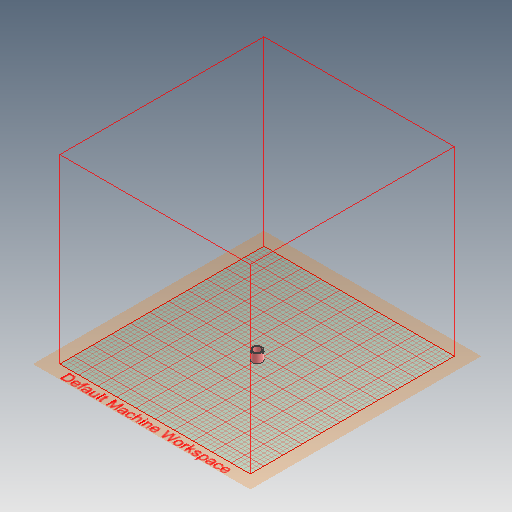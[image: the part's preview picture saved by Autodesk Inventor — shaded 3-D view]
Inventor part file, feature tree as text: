
AUTODESK INVENTOR PART (.ipt)
format: ipt  version: 2021 (Build 250183000, 183)  size: 417,792 bytes
history: native  units: mm
features: sketch x5, extrude x3, other x2, hole x1
ambient origin geometry x8: Origin, YZ Plane, XZ Plane, XY Plane, X Axis, Y Axis, Z Axis, Center Point
bodies: Body1 (feature_tree)
feature tree (11):
  other  "Sólido1"
  other  "Revolução1"
  extrude  "Extrusão1"  Depth=2.0mm
  extrude  "Extrusão4"  TaperAngle=90.0deg  [1 undecoded]
  hole  "Furo1"  [1 undecoded]
  extrude  "Extrusão5"  Depth=20.0mm
  sketch  "Esboço1"  dims[d0=18.0mm d1=2.0mm]
  sketch  "Esboço2"  dims[d2=4.0mm d7=90.0deg]
  sketch  "Esboço5"  dims[d10=45.0deg d11=1.0mm]
  sketch  "Esboço6"  dims[d12=7.0mm d13=12.7mm d14=2.5mm d15=16.5mm d16=0.0mm d30=20.0mm]
  sketch  "Esboço7"  dims[d32=2.5mm d38=10.0mm d39=0.0mm d45=12.0mm d46=3.5mm d47=0.0mm d48=5.0mm d49=45.0deg d50=16.5mm d51=2.85mm d52=14.0mm d53=4.0mm d54=2.0mm d55=90.0deg d56=8.8mm d57=0.0mm]
note: 2 required parameter values undecoded (feature->parameter linkage not recoverable at this tier; creation-order binding heuristic only, values carry confidence <= 0.55)
